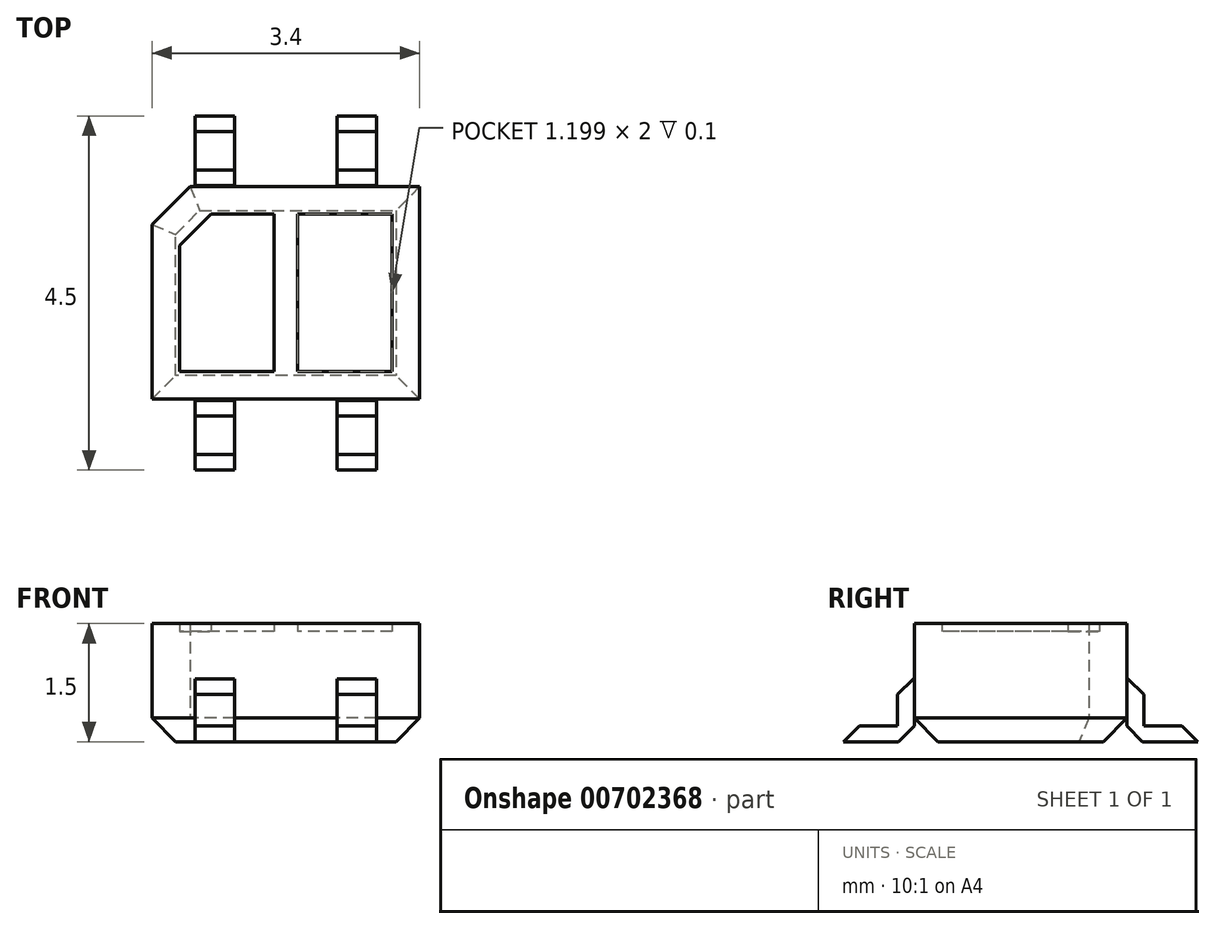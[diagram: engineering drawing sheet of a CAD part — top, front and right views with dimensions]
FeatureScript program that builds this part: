
annotation { "Feature Type Name" : "Feature", "Feature Type Description" : "" }
export const myFeature = defineFeature(function(context is Context, id is Id, definition is map)
    precondition{}
    {
        {
            var Q0;
            Q0=qCreatedBy(makeId("Top.planeOp"),FACE);
            var sketch = newSketch(context, id + "F0", { "sketchPlane" : qUnion([Q0])});
            skLineSegment(sketch, "E0.bottom", {"start": v(1.7, 1.35) * mm, "end": v(-1.22, 1.35) * mm});
            skLineSegment(sketch, "E0.top", {"start": v(1.7, -1.35) * mm, "end": v(-1.7, -1.35) * mm});
            skLineSegment(sketch, "E0.left", {"start": v(1.7, 1.35) * mm, "end": v(1.7, -1.35) * mm});
            skLineSegment(sketch, "E0.right", {"start": v(-1.7, 0.87) * mm, "end": v(-1.7, -1.35) * mm});
            skPoint(sketch, "E0.middle", {"position": v(0, 0) * mm});
            skLineSegment(sketch, "E1.bottom", {"start": v(1.35, 1) * mm, "end": v(0.15, 1) * mm});
            skLineSegment(sketch, "E1.top", {"start": v(1.35, -1) * mm, "end": v(0.15, -1) * mm});
            skLineSegment(sketch, "E1.left", {"start": v(1.35, 1) * mm, "end": v(1.35, -1) * mm});
            skLineSegment(sketch, "E1.right", {"start": v(-1.35, 0.6) * mm, "end": v(-1.35, -1) * mm});
            skLineSegment(sketch, "E2", {"start": v(-1.35, 0.6) * mm, "end": v(-0.95, 1) * mm});
            skPoint(sketch, "E3.orphan", {"position": v(-1.35, 1) * mm});
            skLineSegment(sketch, "E4", {"start": v(-0.15, 1) * mm, "end": v(-0.15, -1) * mm});
            skLineSegment(sketch, "E5.MirrorCS", {"start": v(0.15, 1) * mm, "end": v(0.15, -1) * mm});
            skLineSegment(sketch, "E6.trimOffspring", {"start": v(-0.15, 1) * mm, "end": v(-0.95, 1) * mm});
            skLineSegment(sketch, "E7.trimOffspring", {"start": v(-0.15, -1) * mm, "end": v(-1.35, -1) * mm});
            skLineSegment(sketch, "E8", {"start": v(-1.7, 0.87) * mm, "end": v(-1.22, 1.35) * mm});
            skPoint(sketch, "E9.orphan", {"position": v(-1.7, 1.35) * mm});
            skLineSegment(sketch, "E10", {"start": v(0.65, 2.25) * mm, "end": v(1.15, 2.25) * mm});
            skLineSegment(sketch, "E11", {"start": v(0.65, 2.25) * mm, "end": v(0.65, 1.35) * mm});
            skLineSegment(sketch, "E12", {"start": v(1.15, 2.25) * mm, "end": v(1.15, 1.35) * mm});
            skLineSegment(sketch, "E13.MirrorCS", {"start": v(-0.65, 2.25) * mm, "end": v(-0.65, 1.35) * mm});
            skLineSegment(sketch, "E14.MirrorCS", {"start": v(-0.65, 2.25) * mm, "end": v(-1.15, 2.25) * mm});
            skLineSegment(sketch, "E15.MirrorCS", {"start": v(-1.15, 2.25) * mm, "end": v(-1.15, 1.35) * mm});
            skLineSegment(sketch, "E16.MirrorCS", {"start": v(0.65, -2.25) * mm, "end": v(0.65, -1.35) * mm});
            skLineSegment(sketch, "E17.MirrorCS", {"start": v(-0.65, -2.25) * mm, "end": v(-0.65, -1.35) * mm});
            skLineSegment(sketch, "E18.MirrorCS", {"start": v(-1.15, -2.25) * mm, "end": v(-1.15, -1.35) * mm});
            skLineSegment(sketch, "E19.MirrorCS", {"start": v(-0.65, -2.25) * mm, "end": v(-1.15, -2.25) * mm});
            skLineSegment(sketch, "E20.MirrorCS", {"start": v(0.65, -2.25) * mm, "end": v(1.15, -2.25) * mm});
            skLineSegment(sketch, "E21.MirrorCS", {"start": v(1.15, -2.25) * mm, "end": v(1.15, -1.35) * mm});
            skLineSegment(sketch, "E22", {"start": v(0.65, 1.56) * mm, "end": v(1.15, 1.56) * mm});
            skLineSegment(sketch, "E23.MirrorCS", {"start": v(-0.65, 1.56) * mm, "end": v(-1.15, 1.56) * mm});
            skLineSegment(sketch, "E24.MirrorCS", {"start": v(0.65, -1.56) * mm, "end": v(1.15, -1.56) * mm});
            skLineSegment(sketch, "E25.MirrorCS", {"start": v(-0.65, -1.56) * mm, "end": v(-1.15, -1.56) * mm});
            skSolve(sketch);
        }
        {
            var Q0;
            Q0=makeQuery(id+"F0.imprint","IMPRINT",FACE,{"disambiguationData":[TD([[makeQuery(id+"F0.imprint","IMPRINT",EDGE,{"derivedFrom":sQuery(id+"F0.wireOp",EDGE,"E0.bottom")}),1.0]])]});
            extrude(context, id + "F1", {"entities" : qUnion([Q0]), "depth" : 1.5 * mm, "offsetDistance" : 25 * mm});
        }
        {
            var Q0;
            Q0=makeQuery(id+"F0.imprint","IMPRINT",FACE,{"disambiguationData":[TD([[makeQuery(id+"F0.imprint","IMPRINT",EDGE,{"derivedFrom":sQuery(id+"F0.wireOp",EDGE,"E1.right")}),1.0]])]});
            var Q1;
            Q1=makeQuery(id+"F0.imprint","IMPRINT",FACE,{"disambiguationData":[TD([[makeQuery(id+"F0.imprint","IMPRINT",EDGE,{"derivedFrom":sQuery(id+"F0.wireOp",EDGE,"E1.bottom")}),1.0]])]});
            extrude(context, id + "F2", {"entities" : qUnion([Q0, Q1]), "operationType" : NewBodyOperationType.ADD, "depth" : 1.4 * mm, "offsetDistance" : 25 * mm});
        }
        {
            var Q0;
            Q0=makeQuery(id+"F1.opExtrude","CAP_EDGE",EDGE,{"disambiguationData":[OSD([sQuery(id+"F0.wireOp",EDGE,"E0.right")])],"isStart":true});
            var Q1;
            Q1=makeQuery(id+"F1.opExtrude","CAP_EDGE",EDGE,{"disambiguationData":[OSD([sQuery(id+"F0.wireOp",EDGE,"E8")])],"isStart":true});
            var Q2;
            Q2=makeQuery(id+"F1.opExtrude","CAP_EDGE",EDGE,{"disambiguationData":[OSD([sQuery(id+"F0.wireOp",EDGE,"E0.bottom")])],"isStart":true});
            var Q3;
            Q3=makeQuery(id+"F1.opExtrude","CAP_EDGE",EDGE,{"disambiguationData":[OSD([sQuery(id+"F0.wireOp",EDGE,"E0.top")])],"isStart":true});
            var Q4;
            Q4=makeQuery(id+"F1.opExtrude","CAP_EDGE",EDGE,{"disambiguationData":[OSD([sQuery(id+"F0.wireOp",EDGE,"E0.left")])],"isStart":true});
            chamfer(context, id + "F3", {"entities" : qUnion([Q0, Q1, Q2, Q3, Q4]), "width" : 0.3 * mm, "tangentPropagation" : true});
        }
        {
            var Q0;
            {var subQ0=sQuery(id+"F0.wireOp",EDGE,"E13.MirrorCS");Q0=makeQuery(id+"F0.imprint","IMPRINT",FACE,{"disambiguationData":[TD([[makeQuery(id+"F0.imprint","IMPRINT",EDGE,{"derivedFrom":subQ0}),-1.0]])]});}
            var Q1;
            Q1=makeQuery(id+"F0.imprint","IMPRINT",FACE,{"disambiguationData":[TD([[makeQuery(id+"F0.imprint","IMPRINT",EDGE,{"derivedFrom":sQuery(id+"F0.wireOp",EDGE,"E10")}),-1.0]])]});
            var Q2;
            {var subQ0=sQuery(id+"F0.wireOp",EDGE,"E17.MirrorCS");Q2=makeQuery(id+"F0.imprint","IMPRINT",FACE,{"disambiguationData":[TD([[makeQuery(id+"F0.imprint","IMPRINT",EDGE,{"derivedFrom":subQ0}),1.0]])]});}
            var Q3;
            {var subQ0=sQuery(id+"F0.wireOp",EDGE,"E16.MirrorCS");Q3=makeQuery(id+"F0.imprint","IMPRINT",FACE,{"disambiguationData":[TD([[makeQuery(id+"F0.imprint","IMPRINT",EDGE,{"derivedFrom":subQ0}),-1.0]])]});}
            extrude(context, id + "F4", {"entities" : qUnion([Q0, Q1, Q2, Q3]), "depth" : 0.2 * mm, "offsetDistance" : 25 * mm});
        }
        {
            var Q0;
            {var subQ5=sQuery(id+"F0.wireOp",EDGE,"E22");Q0=makeQuery(id+"F0.imprint","IMPRINT",FACE,{"disambiguationData":[TD([[makeQuery(id+"F0.imprint","IMPRINT",EDGE,{"derivedFrom":subQ5}),-1.0]])]});}
            var Q1;
            {var subQ5=sQuery(id+"F0.wireOp",EDGE,"E23.MirrorCS");Q1=makeQuery(id+"F0.imprint","IMPRINT",FACE,{"disambiguationData":[TD([[makeQuery(id+"F0.imprint","IMPRINT",EDGE,{"derivedFrom":subQ5}),1.0]])]});}
            var Q2;
            {var subQ5=sQuery(id+"F0.wireOp",EDGE,"E25.MirrorCS");Q2=makeQuery(id+"F0.imprint","IMPRINT",FACE,{"disambiguationData":[TD([[makeQuery(id+"F0.imprint","IMPRINT",EDGE,{"derivedFrom":subQ5}),-1.0]])]});}
            var Q3;
            {var subQ5=sQuery(id+"F0.wireOp",EDGE,"E24.MirrorCS");Q3=makeQuery(id+"F0.imprint","IMPRINT",FACE,{"disambiguationData":[TD([[makeQuery(id+"F0.imprint","IMPRINT",EDGE,{"derivedFrom":subQ5}),1.0]])]});}
            extrude(context, id + "F5", {"entities" : qUnion([Q0, Q1, Q2, Q3]), "operationType" : NewBodyOperationType.ADD, "depth" : 0.8 * mm, "offsetDistance" : 25 * mm});
        }
        {
            var Q0;
            Q0=makeQuery(id+"F4.opExtrude","CAP_EDGE",EDGE,{"disambiguationData":[OSD([sQuery(id+"F0.wireOp",EDGE,"E19.MirrorCS")])],"isStart":false});
            var Q1;
            Q1=makeQuery(id+"F4.opExtrude","CAP_EDGE",EDGE,{"disambiguationData":[OSD([sQuery(id+"F0.wireOp",EDGE,"E20.MirrorCS")])],"isStart":false});
            var Q2;
            {var subQ0=sQuery(id+"F0.wireOp",EDGE,"E0.top");Q2=makeQuery(id+"F4.opExtrude","CAP_EDGE",EDGE,{"disambiguationData":[OSD([subQ0]),TDD([makeQuery(id+"F0.imprint","IMPRINT",EDGE,{"disambiguationData":[TD([[makeQuery(id+"F0.imprint","INTERSECT",VERTEX,{"derivedFrom":[subQ0,sQuery(id+"F0.wireOp",EDGE,"E17.MirrorCS")]}),-1.0]])],"derivedFrom":subQ0})])],"isStart":true});}
            var Q3;
            {var subQ0=sQuery(id+"F0.wireOp",EDGE,"E0.top");Q3=makeQuery(id+"F4.opExtrude","CAP_EDGE",EDGE,{"disambiguationData":[OSD([subQ0]),TDD([makeQuery(id+"F0.imprint","IMPRINT",EDGE,{"disambiguationData":[TD([[makeQuery(id+"F0.imprint","INTERSECT",VERTEX,{"derivedFrom":[subQ0,sQuery(id+"F0.wireOp",EDGE,"E16.MirrorCS")]}),1.0]])],"derivedFrom":subQ0})])],"isStart":true});}
            var Q4;
            {var subQ0=sQuery(id+"F0.wireOp",EDGE,"E0.bottom");Q4=makeQuery(id+"F5.opExtrude","CAP_EDGE",EDGE,{"disambiguationData":[OSD([subQ0]),TDD([makeQuery(id+"F0.imprint","IMPRINT",EDGE,{"disambiguationData":[TD([[makeQuery(id+"F0.imprint","INTERSECT",VERTEX,{"derivedFrom":[subQ0,sQuery(id+"F0.wireOp",EDGE,"E11")]}),1.0]])],"derivedFrom":subQ0})])],"isStart":true});}
            var Q5;
            Q5=makeQuery(id+"F4.opExtrude","CAP_EDGE",EDGE,{"disambiguationData":[OSD([sQuery(id+"F0.wireOp",EDGE,"E14.MirrorCS")])],"isStart":false});
            var Q6;
            Q6=makeQuery(id+"F4.opExtrude","CAP_EDGE",EDGE,{"disambiguationData":[OSD([sQuery(id+"F0.wireOp",EDGE,"E10")])],"isStart":false});
            var Q7;
            Q7=makeQuery(id+"F4.opExtrude","CAP_EDGE",EDGE,{"disambiguationData":[OSD([sQuery(id+"F0.wireOp",EDGE,"E0.bottom")])],"isStart":true});
            var Q8;
            Q8=makeQuery(id+"F5.opExtrude","CAP_EDGE",EDGE,{"disambiguationData":[OSD([sQuery(id+"F0.wireOp",EDGE,"E22")])],"isStart":false});
            var Q9;
            Q9=makeQuery(id+"F5.opExtrude","CAP_EDGE",EDGE,{"disambiguationData":[OSD([sQuery(id+"F0.wireOp",EDGE,"E23.MirrorCS")])],"isStart":false});
            var Q10;
            Q10=makeQuery(id+"F5.opExtrude","CAP_EDGE",EDGE,{"disambiguationData":[OSD([sQuery(id+"F0.wireOp",EDGE,"E25.MirrorCS")])],"isStart":false});
            var Q11;
            Q11=makeQuery(id+"F5.opExtrude","CAP_EDGE",EDGE,{"disambiguationData":[OSD([sQuery(id+"F0.wireOp",EDGE,"E24.MirrorCS")])],"isStart":false});
            chamfer(context, id + "F6", {"entities" : qUnion([Q0, Q1, Q2, Q3, Q4, Q5, Q6, Q7, Q8, Q9, Q10, Q11]), "width" : 0.2 * mm, "tangentPropagation" : true});
        }
    });
